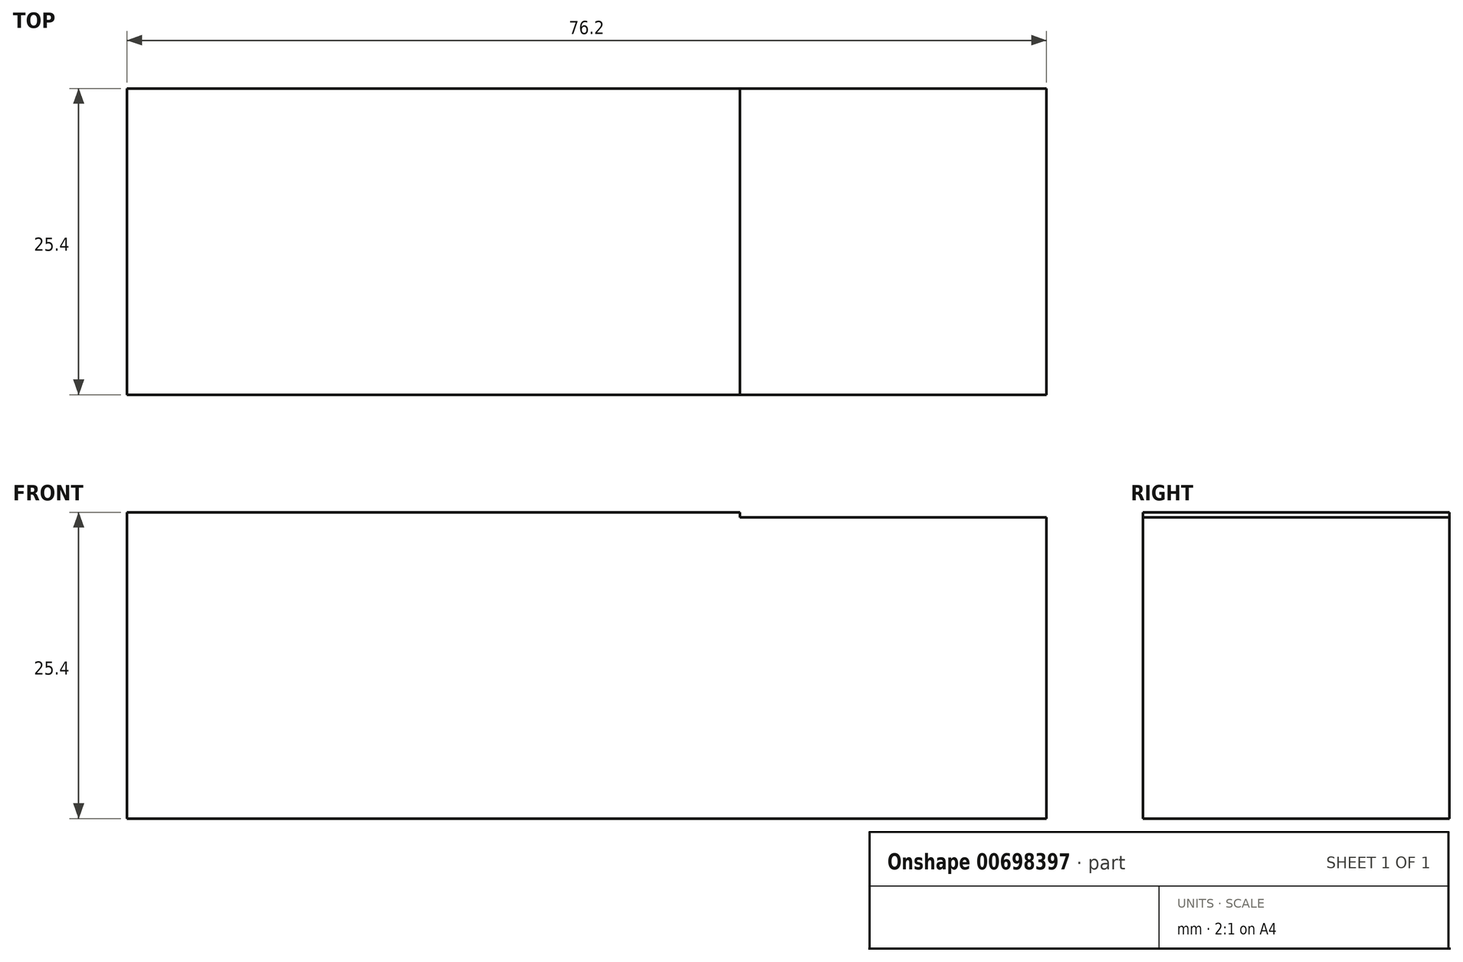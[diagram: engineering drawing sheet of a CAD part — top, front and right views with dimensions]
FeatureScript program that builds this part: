
annotation { "Feature Type Name" : "Feature", "Feature Type Description" : "" }
export const myFeature = defineFeature(function(context is Context, id is Id, definition is map)
    precondition{}
    {
        {
            var Q0;
            Q0=qCreatedBy(makeId("Front.planeOp"),FACE);
            var sketch = newSketch(context, id + "F0", { "sketchPlane" : qUnion([Q0])});
            skLineSegment(sketch, "E0.bottom", {"start": v(0, 0) * mm, "end": v(-25.4, 0) * mm});
            skLineSegment(sketch, "E0.top", {"start": v(0, 25.4) * mm, "end": v(-25.4, 25.4) * mm});
            skLineSegment(sketch, "E0.left", {"start": v(0, 0) * mm, "end": v(0, 25.4) * mm});
            skLineSegment(sketch, "E0.right", {"start": v(-25.4, 0) * mm, "end": v(-25.4, 25.4) * mm});
            skLineSegment(sketch, "E1.bottom", {"start": v(0, 0) * mm, "end": v(25.4, 0) * mm});
            skLineSegment(sketch, "E1.top", {"start": v(0, 24.96) * mm, "end": v(25.4, 24.96) * mm});
            skLineSegment(sketch, "E1.left", {"start": v(0, 0) * mm, "end": v(0, 24.96) * mm});
            skLineSegment(sketch, "E1.right", {"start": v(25.4, 0) * mm, "end": v(25.4, 24.96) * mm});
            skLineSegment(sketch, "E2.bottom", {"start": v(-25.4, 25.4) * mm, "end": v(-50.8, 25.4) * mm});
            skLineSegment(sketch, "E2.top", {"start": v(-25.4, 0) * mm, "end": v(-50.8, 0) * mm});
            skLineSegment(sketch, "E2.left", {"start": v(-25.4, 25.4) * mm, "end": v(-25.4, 0) * mm});
            skLineSegment(sketch, "E2.right", {"start": v(-50.8, 25.4) * mm, "end": v(-50.8, 0) * mm});
            skLineSegment(sketch, "E3.bottom", {"start": v(-25.4, 25.4) * mm, "end": v(0, 25.4) * mm});
            skLineSegment(sketch, "E3.top", {"start": v(-25.4, 50.8) * mm, "end": v(0, 50.8) * mm});
            skLineSegment(sketch, "E3.left", {"start": v(-25.4, 25.4) * mm, "end": v(-25.4, 50.8) * mm});
            skLineSegment(sketch, "E3.right", {"start": v(0, 25.4) * mm, "end": v(0, 50.8) * mm});
            skSolve(sketch);
        }
        {
            var Q0;
            Q0=makeQuery(id+"F0.imprint","IMPRINT",FACE,{"disambiguationData":[TD([[makeQuery(id+"F0.imprint","IMPRINT",EDGE,{"derivedFrom":sQuery(id+"F0.wireOp",EDGE,"E2.bottom")}),1.0]])]});
            var Q1;
            Q1=makeQuery(id+"F0.imprint","IMPRINT",FACE,{"disambiguationData":[TD([[makeQuery(id+"F0.imprint","IMPRINT",EDGE,{"derivedFrom":sQuery(id+"F0.wireOp",EDGE,"E0.bottom")}),-1.0]])]});
            var Q2;
            Q2=makeQuery(id+"F0.imprint","IMPRINT",FACE,{"disambiguationData":[TD([[makeQuery(id+"F0.imprint","IMPRINT",EDGE,{"derivedFrom":sQuery(id+"F0.wireOp",EDGE,"E1.bottom")}),1.0]])]});
            var Q3;
            Q3=makeQuery(id+"F0.imprint","IMPRINT",FACE,{"disambiguationData":[TD([[makeQuery(id+"F0.imprint","IMPRINT",EDGE,{"derivedFrom":sQuery(id+"F0.wireOp",EDGE,"E3.bottom")}),1.0]])]});
            extrude(context, id + "F1", {"entities" : qUnion([Q0, Q1, Q2, Q3]), "depth" : 25.4 * mm, "offsetDistance" : 25.4 * mm});
        }
    });
